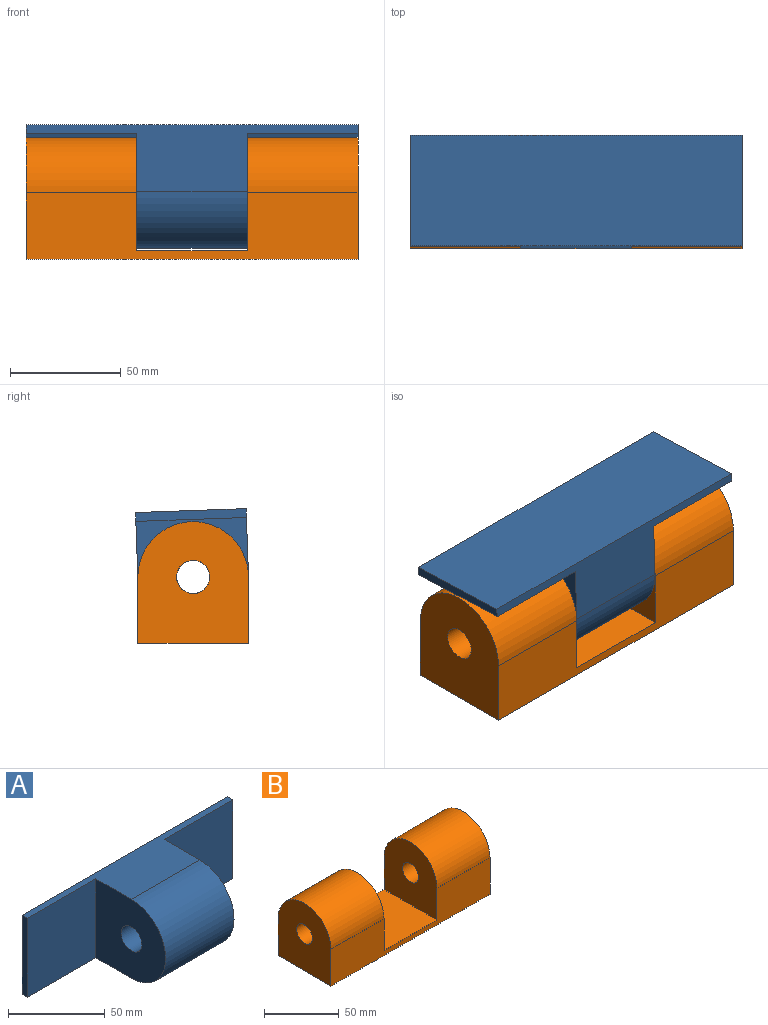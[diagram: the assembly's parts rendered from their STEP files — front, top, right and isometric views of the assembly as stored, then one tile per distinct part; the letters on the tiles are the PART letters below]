
ASSEMBLY  parts=2 mates=1
PART A: 11 faces, bbox 150x55x50 mm
  f0: plane 150x30mm, normal (0,0,1), area 1900mm2, adj f2,f3,f4,f5,f6,f7,f8,f9
  f1: plane 150x30mm, normal (0,0,-1), area 1900mm2, adj f2,f3,f4,f5,f6,f7,f8,f9
  f2: cylinder r=25mm len=50mm, axis (-1,0,0), area 3927mm2, adj f0,f1,f7,f9
  f3: plane 150x50mm, normal (0,1,0), area 7500mm2, adj f0,f1,f4,f5
  f4: plane 50x4mm, normal (1,0,0), area 200mm2, adj f0,f1,f3,f8
  f5: plane 50x4mm, normal (-1,0,0), area 200mm2, adj f0,f1,f3,f6
  f6: plane 50x50mm, normal (0,-1,0), area 2500mm2, adj f0,f1,f5,f7
  f7: plane 51x50mm, normal (-1,0,0), area 2105mm2, adj f0,f1,f2,f6,f10
  f8: plane 50x50mm, normal (0,-1,0), area 2500mm2, adj f0,f1,f4,f9
  f9: plane 51x50mm, normal (1,0,0), area 2105mm2, adj f0,f1,f2,f8,f10
  f10: cylinder r=7.5mm len=50mm, axis (1,0,0), area 2356.2mm2, adj f7,f9
PART B: 12 faces, bbox 150x50x55 mm
  f0: cylinder r=25mm len=50mm, axis (-1,0,0), area 3927mm2, adj f1,f2,f4,f9
  f1: plane 150x30mm, normal (0,1,0), area 3200mm2, adj f0,f3,f4,f5,f6,f7,f8,f9
  f2: plane 150x30mm, normal (0,-1,0), area 3200mm2, adj f0,f3,f4,f5,f6,f7,f8,f9
  f3: plane 150x50mm, normal (0,0,-1), area 7500mm2, adj f1,f2,f4,f5
  f4: plane 55x50mm, normal (1,0,0), area 2305mm2, adj f0,f1,f2,f3,f10
  f5: plane 55x50mm, normal (-1,0,0), area 2305mm2, adj f1,f2,f3,f6,f11
  f6: cylinder r=25mm len=50mm, axis (-1,0,0), area 3927mm2, adj f1,f2,f5,f8
  f7: plane 50x50mm, normal (0,0,1), area 2500mm2, adj f1,f2,f8,f9
  f8: plane 51x50mm, normal (1,0,0), area 2105mm2, adj f1,f2,f6,f7,f11
  f9: plane 51x50mm, normal (-1,0,0), area 2105mm2, adj f0,f1,f2,f7,f10
  f10: cylinder r=7.5mm len=50mm, axis (1,0,0), area 2356.2mm2, adj f4,f9
  f11: cylinder r=7.5mm len=50mm, axis (1,0,0), area 2356.2mm2, adj f5,f8
PLACE A rot(axis=(1,0,0),88deg) t=(0,-2.41,2.5)mm
PLACE B at identity fixed
MATE revolute A.f2 <-> B.f0  axis (-1,0,0) through (100,-2.5,0)mm
